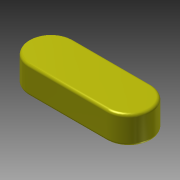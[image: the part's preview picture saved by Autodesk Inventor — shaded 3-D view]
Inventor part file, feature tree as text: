
AUTODESK INVENTOR PART (.ipt)
format: ipt  version: 2015 (Build 190159000, 159)  size: 110,080 bytes
history: native  units: mm
features: extrude x1, fillet x1, sketch x1
ambient origin geometry x8: Origin, YZ Plane, XZ Plane, XY Plane, X Axis, Y Axis, Z Axis, Center Point
bodies: 实体1 (feature_tree)
feature tree (3):
  extrude  "拉伸1"  Depth=8.0mm
  fillet  "圆角1"  Radius=5.0mm
  sketch  "草图1"  dims[d0=14.0mm d1=8.0mm d2=5.0mm d3=0.0mm d4=0.5mm]
